AUTODESK INVENTOR PART (.ipt)
format: ipt  version: 2015 SP1 (Build 190203100, 203)  size: 207,872 bytes
history: native  units: in
note: dims shown in document units (in); Inventor stores cm internally (conversion verified against a paired STEP export)
features: sketch x2, extrude x1, hole x1, fillet x1
ambient origin geometry x8: Origin, YZ Plane, XZ Plane, XY Plane, X Axis, Y Axis, Z Axis, Center Point
bodies: Solid1 (feature_tree)
feature tree (5):
  extrude  "Extrusion1"  Depth=17.0in
  hole  "Hole1"  [1 undecoded]
  fillet  "Fillet1"  Radius=3.5in
  sketch  "Sketch1"  dims[d0=8.5in d1=17.0in]
  sketch  "Sketch2"  dims[d2=0.1875in d3=0.0in d4=0.163in d5=0.75in d6=0.375in d7=0.25in d8=0.5635in d9=1.0in d10=0.8108in d11=0.125in d12=3.5in d13=0.5in d14=1.0in d15=0.5in d16=4.3307in d18=1.0in d19=0.3937in d21=1.0in d23=1.9685in d25=2.0in d26=0.3937in d28=1.0in d30=1.0in d31=0.5in d32=1.0in d33=0.5in d34=1.5748in d36=2.0in d37=0.3937in d39=1.0in]
note: 1 required parameter value undecoded (feature->parameter linkage not recoverable at this tier; creation-order binding heuristic only, values carry confidence <= 0.55)
